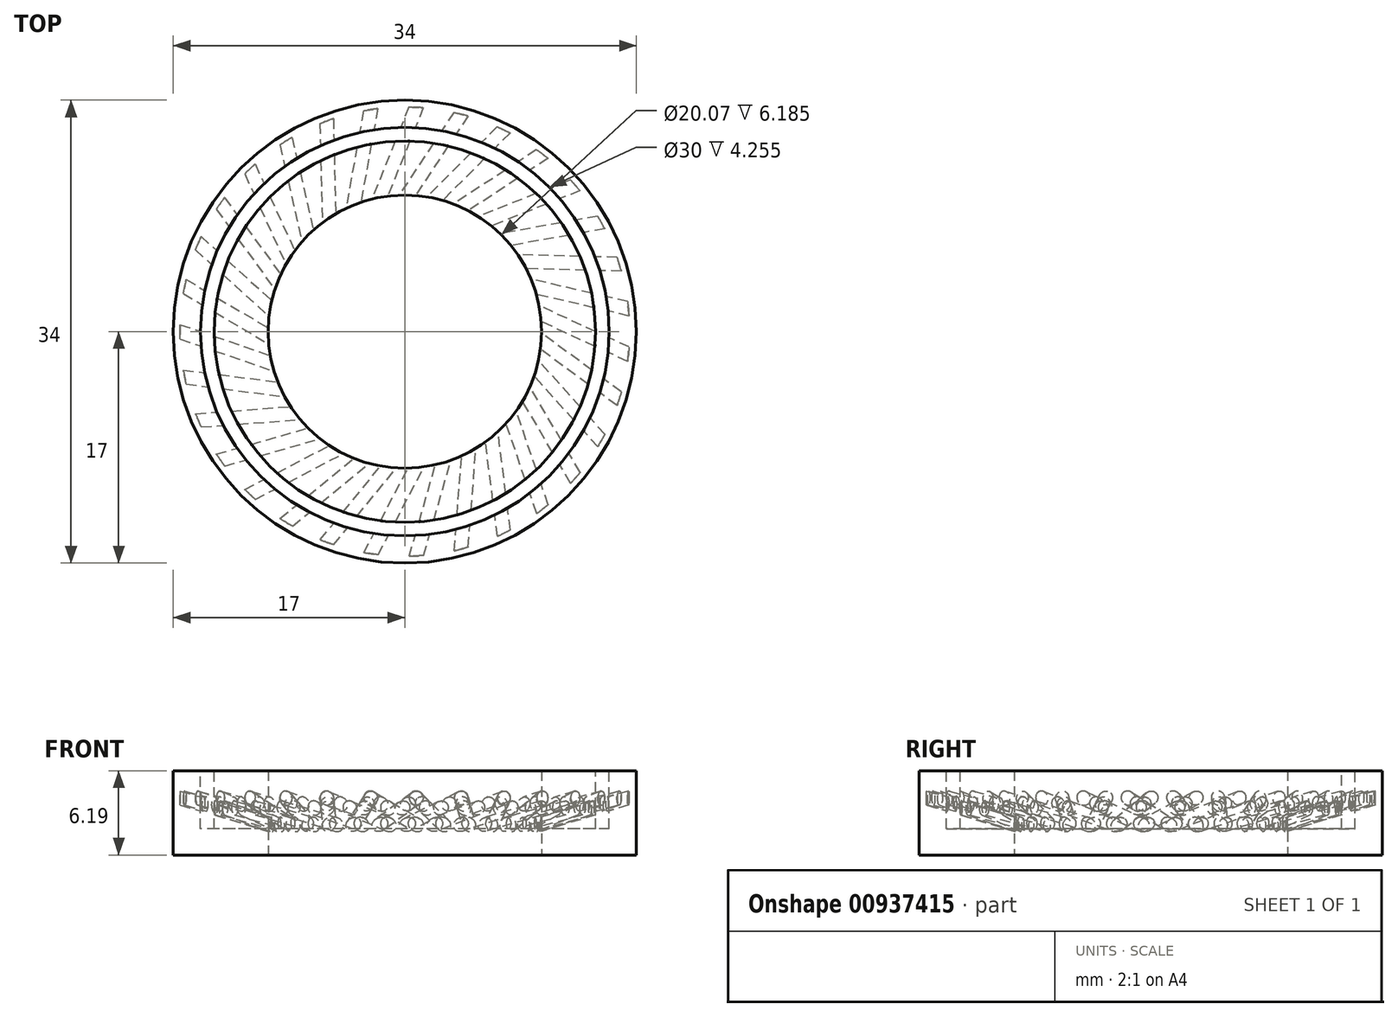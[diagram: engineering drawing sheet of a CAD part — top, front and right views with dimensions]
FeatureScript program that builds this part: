
annotation { "Feature Type Name" : "Feature", "Feature Type Description" : "" }
export const myFeature = defineFeature(function(context is Context, id is Id, definition is map)
    precondition{}
    {
        {
            var Q0;
            Q0=qCreatedBy(makeId("Top.planeOp"),FACE);
            var sketch = newSketch(context, id + "F0", { "sketchPlane" : qUnion([Q0])});
            skCircle(sketch, "E0", {"center": v(0, 0) * mm, "radius": 16.5 * mm});
            skSolve(sketch);
        }
        {
            var Q0;
            Q0=makeQuery(id+"F0.imprint","IMPRINT",FACE,{"disambiguationData":[TD([[makeQuery(id+"F0.imprint","IMPRINT",EDGE,{"derivedFrom":sQuery(id+"F0.wireOp",EDGE,"E0")}),1.0]])]});
            extrude(context, id + "F1", {"entities" : qUnion([Q0]), "depth" : 7.94 * mm, "offsetDistance" : 25.4 * mm});
        }
        {
            var Q0;
            Q0=qCreatedBy(makeId("Top.planeOp"),FACE);
            var sketch = newSketch(context, id + "F2", { "sketchPlane" : qUnion([Q0])});
            skCircle(sketch, "E1", {"center": v(0, 0) * mm, "radius": 10.03 * mm});
            skSolve(sketch);
        }
        {
            var Q0;
            Q0=qSketchRegion(id+"F2",true);
            extrude(context, id + "F3", {"entities" : qUnion([Q0]), "operationType" : NewBodyOperationType.REMOVE, "depth" : 7.94 * mm, "offsetDistance" : 25.4 * mm});
        }
        {
            var Q0;
            Q0=qCreatedBy(makeId("Right.planeOp"),FACE);
            var sketch = newSketch(context, id + "F4", { "sketchPlane" : qUnion([Q0])});
            skLineSegment(sketch, "E2", {"start": v(0, 0) * mm, "end": v(0, 143.33) * mm});
            skLineSegment(sketch, "E3", {"start": v(-8.9, 0) * mm, "end": v(-8.9, 70.97) * mm});
            skSolve(sketch);
        }
        {
            var Q0;
            Q0=qCreatedBy(makeId("Top.planeOp"),FACE);
            var sketch = newSketch(context, id + "F5", { "sketchPlane" : qUnion([Q0])});
            skLineSegment(sketch, "E4", {"start": v(0, 0) * mm, "end": v(29.86, 0) * mm});
            skSolve(sketch);
        }
        {
            var Q0;
            Q0=qCreatedBy(makeId("Right.planeOp"),FACE);
            var sketch = newSketch(context, id + "F6", { "sketchPlane" : qUnion([Q0])});
            skCircle(sketch, "E5", {"center": v(0, 54.1) * mm, "radius": 0.5 * mm});
            skSolve(sketch);
        }
        {
            var Q0;
            Q0=makeQuery(id+"F6.imprint","IMPRINT",FACE,{"disambiguationData":[TD([[makeQuery(id+"F6.imprint","IMPRINT",EDGE,{"derivedFrom":sQuery(id+"F6.wireOp",EDGE,"E5")}),1.0]])]});
            extrude(context, id + "F7", {"entities" : qUnion([Q0]), "depth" : 25.4 * mm, "offsetDistance" : 25.4 * mm});
        }
        {
            var Q0;
            Q0=makeQuery(id+"F7.opExtrude","SWEPT_BODY",BODY,{"disambiguationData":[OSD([sQuery(id+"F6.wireOp",EDGE,"E5")])]});
            var Q1;
            Q1=sQuery(id+"F4.wireOp",EDGE,"E2");
            transform(context, id + "F8", {"entities" : qUnion([Q0]), "transformType" : TransformType.ROTATION, "transformAxis" : qUnion([Q1]), "angle" : 20 * degree, "makeCopy" : false});
        }
        {
            var Q0;
            Q0=makeQuery(id+"F7.opExtrude","SWEPT_BODY",BODY,{"disambiguationData":[OSD([sQuery(id+"F6.wireOp",EDGE,"E5")])]});
            transform(context, id + "F9", {"entities" : qUnion([Q0]), "transformType" : TransformType.TRANSLATION_3D, "dx" : 0 * mm, "dy" : 0 * mm, "dz" : -54.1 * mm, "makeCopy" : false});
        }
        {
            var Q0;
            Q0=makeQuery(id+"F7.opExtrude","SWEPT_BODY",BODY,{"disambiguationData":[OSD([sQuery(id+"F6.wireOp",EDGE,"E5")])]});
            var Q1;
            Q1=sQuery(id+"F5.wireOp",EDGE,"E4");
            var Q2;
            Q2=sQuery(id+"F5.wireOp",EDGE,"E4");
            transform(context, id + "F10", {"entities" : qUnion([Q0]), "transformType" : TransformType.ROTATION, "transformAxis" : qUnion([Q2]), "angle" : 50 * degree, "makeCopy" : false});
        }
        {
            var Q0;
            Q0=makeQuery(id+"F7.opExtrude","SWEPT_BODY",BODY,{"disambiguationData":[OSD([sQuery(id+"F6.wireOp",EDGE,"E5")])]});
            var Q1;
            Q1=sQuery(id+"F4.wireOp",EDGE,"E2");
            var Q2;
            Q2=sQuery(id+"F4.wireOp",EDGE,"E3");
            transform(context, id + "F11", {"entities" : qUnion([Q0]), "transformType" : TransformType.ROTATION, "transformAxis" : qUnion([Q2]), "angle" : 55 * degree, "makeCopy" : false});
        }
        {
            var Q0;
            Q0=makeQuery(id+"F7.opExtrude","SWEPT_BODY",BODY,{"disambiguationData":[OSD([sQuery(id+"F6.wireOp",EDGE,"E5")])]});
            var Q1;
            Q1=sQuery(id+"F4.wireOp",EDGE,"E2");
            circularPattern(context, id + "F12", {"entities" : qUnion([Q0]), "axis" : qUnion([Q1]), "angle" : 360 * degree, "instanceCount" : 31, "equalSpace" : true});
        }
        {
            var Q0;
            Q0=makeQuery(id+"F7.opExtrude","SWEPT_BODY",BODY,{"disambiguationData":[OSD([sQuery(id+"F6.wireOp",EDGE,"E5")])]});
            var Q1;
            Q1=makeQuery(id+"F12.opPattern","COPY",BODY,{"derivedFrom":makeQuery(id+"F7.opExtrude","SWEPT_BODY",BODY,{"disambiguationData":[OSD([sQuery(id+"F6.wireOp",EDGE,"E5")])]}),"instanceName":"14"});
            var Q2;
            Q2=makeQuery(id+"F1.opExtrude","SWEPT_BODY",BODY,{"disambiguationData":[OSD([sQuery(id+"F0.wireOp",EDGE,"E0")])]});
            booleanBodies(context, id + "F13", {"operationType" : BooleanOperationType.SUBTRACTION, "tools" : qUnion([Q0, Q1]), "targets" : qUnion([Q2])});
        }
        {
            var Q0;
            Q0=makeQuery(id+"F12.opPattern","COPY",BODY,{"derivedFrom":makeQuery(id+"F7.opExtrude","SWEPT_BODY",BODY,{"disambiguationData":[OSD([sQuery(id+"F6.wireOp",EDGE,"E5")])]}),"instanceName":"30"});
            var Q1;
            Q1=makeQuery(id+"F12.opPattern","COPY",BODY,{"derivedFrom":makeQuery(id+"F7.opExtrude","SWEPT_BODY",BODY,{"disambiguationData":[OSD([sQuery(id+"F6.wireOp",EDGE,"E5")])]}),"instanceName":"28"});
            var Q2;
            Q2=makeQuery(id+"F12.opPattern","COPY",BODY,{"derivedFrom":makeQuery(id+"F7.opExtrude","SWEPT_BODY",BODY,{"disambiguationData":[OSD([sQuery(id+"F6.wireOp",EDGE,"E5")])]}),"instanceName":"26"});
            var Q3;
            Q3=makeQuery(id+"F12.opPattern","COPY",BODY,{"derivedFrom":makeQuery(id+"F7.opExtrude","SWEPT_BODY",BODY,{"disambiguationData":[OSD([sQuery(id+"F6.wireOp",EDGE,"E5")])]}),"instanceName":"24"});
            var Q4;
            Q4=makeQuery(id+"F12.opPattern","COPY",BODY,{"derivedFrom":makeQuery(id+"F7.opExtrude","SWEPT_BODY",BODY,{"disambiguationData":[OSD([sQuery(id+"F6.wireOp",EDGE,"E5")])]}),"instanceName":"22"});
            var Q5;
            Q5=makeQuery(id+"F1.opExtrude","SWEPT_BODY",BODY,{"disambiguationData":[OSD([sQuery(id+"F0.wireOp",EDGE,"E0")])]});
            booleanBodies(context, id + "F14", {"operationType" : BooleanOperationType.SUBTRACTION, "tools" : qUnion([Q0, Q1, Q2, Q3, Q4]), "targets" : qUnion([Q5])});
        }
        {
            var Q0;
            Q0=makeQuery(id+"F12.opPattern","COPY",BODY,{"derivedFrom":makeQuery(id+"F7.opExtrude","SWEPT_BODY",BODY,{"disambiguationData":[OSD([sQuery(id+"F6.wireOp",EDGE,"E5")])]}),"instanceName":"20"});
            var Q1;
            Q1=makeQuery(id+"F12.opPattern","COPY",BODY,{"derivedFrom":makeQuery(id+"F7.opExtrude","SWEPT_BODY",BODY,{"disambiguationData":[OSD([sQuery(id+"F6.wireOp",EDGE,"E5")])]}),"instanceName":"18"});
            var Q2;
            Q2=makeQuery(id+"F12.opPattern","COPY",BODY,{"derivedFrom":makeQuery(id+"F7.opExtrude","SWEPT_BODY",BODY,{"disambiguationData":[OSD([sQuery(id+"F6.wireOp",EDGE,"E5")])]}),"instanceName":"16"});
            var Q3;
            Q3=makeQuery(id+"F12.opPattern","COPY",BODY,{"derivedFrom":makeQuery(id+"F7.opExtrude","SWEPT_BODY",BODY,{"disambiguationData":[OSD([sQuery(id+"F6.wireOp",EDGE,"E5")])]}),"instanceName":"13"});
            var Q4;
            Q4=makeQuery(id+"F12.opPattern","COPY",BODY,{"derivedFrom":makeQuery(id+"F7.opExtrude","SWEPT_BODY",BODY,{"disambiguationData":[OSD([sQuery(id+"F6.wireOp",EDGE,"E5")])]}),"instanceName":"11"});
            var Q5;
            Q5=makeQuery(id+"F12.opPattern","COPY",BODY,{"derivedFrom":makeQuery(id+"F7.opExtrude","SWEPT_BODY",BODY,{"disambiguationData":[OSD([sQuery(id+"F6.wireOp",EDGE,"E5")])]}),"instanceName":"9"});
            var Q6;
            Q6=makeQuery(id+"F12.opPattern","COPY",BODY,{"derivedFrom":makeQuery(id+"F7.opExtrude","SWEPT_BODY",BODY,{"disambiguationData":[OSD([sQuery(id+"F6.wireOp",EDGE,"E5")])]}),"instanceName":"7"});
            var Q7;
            Q7=makeQuery(id+"F12.opPattern","COPY",BODY,{"derivedFrom":makeQuery(id+"F7.opExtrude","SWEPT_BODY",BODY,{"disambiguationData":[OSD([sQuery(id+"F6.wireOp",EDGE,"E5")])]}),"instanceName":"5"});
            var Q8;
            Q8=makeQuery(id+"F12.opPattern","COPY",BODY,{"derivedFrom":makeQuery(id+"F7.opExtrude","SWEPT_BODY",BODY,{"disambiguationData":[OSD([sQuery(id+"F6.wireOp",EDGE,"E5")])]}),"instanceName":"3"});
            var Q9;
            Q9=makeQuery(id+"F12.opPattern","COPY",BODY,{"derivedFrom":makeQuery(id+"F7.opExtrude","SWEPT_BODY",BODY,{"disambiguationData":[OSD([sQuery(id+"F6.wireOp",EDGE,"E5")])]}),"instanceName":"1"});
            var Q10;
            Q10=makeQuery(id+"F1.opExtrude","SWEPT_BODY",BODY,{"disambiguationData":[OSD([sQuery(id+"F0.wireOp",EDGE,"E0")])]});
            booleanBodies(context, id + "F15", {"operationType" : BooleanOperationType.SUBTRACTION, "tools" : qUnion([Q0, Q1, Q2, Q3, Q4, Q5, Q6, Q7, Q8, Q9]), "targets" : qUnion([Q10])});
        }
        {
            var Q0;
            Q0=makeQuery(id+"F12.opPattern","COPY",BODY,{"derivedFrom":makeQuery(id+"F7.opExtrude","SWEPT_BODY",BODY,{"disambiguationData":[OSD([sQuery(id+"F6.wireOp",EDGE,"E5")])]}),"instanceName":"29"});
            var Q1;
            Q1=makeQuery(id+"F12.opPattern","COPY",BODY,{"derivedFrom":makeQuery(id+"F7.opExtrude","SWEPT_BODY",BODY,{"disambiguationData":[OSD([sQuery(id+"F6.wireOp",EDGE,"E5")])]}),"instanceName":"27"});
            var Q2;
            Q2=makeQuery(id+"F12.opPattern","COPY",BODY,{"derivedFrom":makeQuery(id+"F7.opExtrude","SWEPT_BODY",BODY,{"disambiguationData":[OSD([sQuery(id+"F6.wireOp",EDGE,"E5")])]}),"instanceName":"25"});
            var Q3;
            Q3=makeQuery(id+"F12.opPattern","COPY",BODY,{"derivedFrom":makeQuery(id+"F7.opExtrude","SWEPT_BODY",BODY,{"disambiguationData":[OSD([sQuery(id+"F6.wireOp",EDGE,"E5")])]}),"instanceName":"23"});
            var Q4;
            Q4=makeQuery(id+"F12.opPattern","COPY",BODY,{"derivedFrom":makeQuery(id+"F7.opExtrude","SWEPT_BODY",BODY,{"disambiguationData":[OSD([sQuery(id+"F6.wireOp",EDGE,"E5")])]}),"instanceName":"21"});
            var Q5;
            Q5=makeQuery(id+"F12.opPattern","COPY",BODY,{"derivedFrom":makeQuery(id+"F7.opExtrude","SWEPT_BODY",BODY,{"disambiguationData":[OSD([sQuery(id+"F6.wireOp",EDGE,"E5")])]}),"instanceName":"19"});
            var Q6;
            Q6=makeQuery(id+"F12.opPattern","COPY",BODY,{"derivedFrom":makeQuery(id+"F7.opExtrude","SWEPT_BODY",BODY,{"disambiguationData":[OSD([sQuery(id+"F6.wireOp",EDGE,"E5")])]}),"instanceName":"17"});
            var Q7;
            Q7=makeQuery(id+"F12.opPattern","COPY",BODY,{"derivedFrom":makeQuery(id+"F7.opExtrude","SWEPT_BODY",BODY,{"disambiguationData":[OSD([sQuery(id+"F6.wireOp",EDGE,"E5")])]}),"instanceName":"15"});
            var Q8;
            Q8=makeQuery(id+"F12.opPattern","COPY",BODY,{"derivedFrom":makeQuery(id+"F7.opExtrude","SWEPT_BODY",BODY,{"disambiguationData":[OSD([sQuery(id+"F6.wireOp",EDGE,"E5")])]}),"instanceName":"12"});
            var Q9;
            Q9=makeQuery(id+"F12.opPattern","COPY",BODY,{"derivedFrom":makeQuery(id+"F7.opExtrude","SWEPT_BODY",BODY,{"disambiguationData":[OSD([sQuery(id+"F6.wireOp",EDGE,"E5")])]}),"instanceName":"10"});
            var Q10;
            Q10=makeQuery(id+"F12.opPattern","COPY",BODY,{"derivedFrom":makeQuery(id+"F7.opExtrude","SWEPT_BODY",BODY,{"disambiguationData":[OSD([sQuery(id+"F6.wireOp",EDGE,"E5")])]}),"instanceName":"8"});
            var Q11;
            Q11=makeQuery(id+"F12.opPattern","COPY",BODY,{"derivedFrom":makeQuery(id+"F7.opExtrude","SWEPT_BODY",BODY,{"disambiguationData":[OSD([sQuery(id+"F6.wireOp",EDGE,"E5")])]}),"instanceName":"6"});
            var Q12;
            Q12=makeQuery(id+"F12.opPattern","COPY",BODY,{"derivedFrom":makeQuery(id+"F7.opExtrude","SWEPT_BODY",BODY,{"disambiguationData":[OSD([sQuery(id+"F6.wireOp",EDGE,"E5")])]}),"instanceName":"4"});
            var Q13;
            Q13=makeQuery(id+"F12.opPattern","COPY",BODY,{"derivedFrom":makeQuery(id+"F7.opExtrude","SWEPT_BODY",BODY,{"disambiguationData":[OSD([sQuery(id+"F6.wireOp",EDGE,"E5")])]}),"instanceName":"2"});
            var Q14;
            Q14=makeQuery(id+"F1.opExtrude","SWEPT_BODY",BODY,{"disambiguationData":[OSD([sQuery(id+"F0.wireOp",EDGE,"E0")])]});
            booleanBodies(context, id + "F16", {"operationType" : BooleanOperationType.SUBTRACTION, "tools" : qUnion([Q0, Q1, Q2, Q3, Q4, Q5, Q6, Q7, Q8, Q9, Q10, Q11, Q12, Q13]), "targets" : qUnion([Q14])});
        }
        {
            var Q0;
            Q0=makeQuery(id+"F1.opExtrude","CAP_FACE",FACE,{"disambiguationData":[OSD([sQuery(id+"F0.wireOp",EDGE,"E0")])],"isStart":true});
            var sketch = newSketch(context, id + "F17", { "sketchPlane" : qUnion([Q0])});
            skCircle(sketch, "E6", {"center": v(0, 0) * mm, "radius": 16.5 * mm});
            skSolve(sketch);
        }
        {
            var Q0;
            Q0=makeQuery(id+"F17.imprint","IMPRINT",FACE,{"disambiguationData":[TD([[makeQuery(id+"F17.imprint","IMPRINT",EDGE,{"derivedFrom":sQuery(id+"F17.wireOp",EDGE,"E6")}),-1.0]])]});
            extrude(context, id + "F18", {"entities" : qUnion([Q0]), "operationType" : NewBodyOperationType.REMOVE, "oppositeDirection" : true, "depth" : 1.75 * mm, "offsetDistance" : 25.4 * mm});
        }
        {
            var Q0;
            Q0=makeQuery(id+"F1.opExtrude","CAP_FACE",FACE,{"disambiguationData":[OSD([sQuery(id+"F0.wireOp",EDGE,"E0")])],"isStart":false});
            var sketch = newSketch(context, id + "F19", { "sketchPlane" : qUnion([Q0])});
            skCircle(sketch, "E7", {"center": v(0, 0) * mm, "radius": 15 * mm});
            skCircle(sketch, "E8", {"center": v(0, 0) * mm, "radius": 14 * mm});
            skSolve(sketch);
        }
        {
            var Q0;
            Q0=makeQuery(id+"F19.imprint","IMPRINT",FACE,{"disambiguationData":[TD([[makeQuery(id+"F19.imprint","IMPRINT",EDGE,{"derivedFrom":sQuery(id+"F19.wireOp",EDGE,"E7")}),1.0]])]});
            var Q1;
            Q1=sQuery(id+"F19.wireOp",EDGE,"E7");
            var Q2;
            Q2=sQuery(id+"F19.wireOp",EDGE,"E8");
            extrude(context, id + "F20", {"entities" : qUnion([Q0]), "operationType" : NewBodyOperationType.REMOVE, "surfaceEntities" : qUnion([Q1, Q2]), "oppositeDirection" : true, "depth" : 4.25 * mm, "offsetDistance" : 25.4 * mm});
        }
        {
            var Q0;
            {var subQ0=sQuery(id+"F0.wireOp",EDGE,"E0");Q0=makeQuery(id+"F20.boolean.opBoolean","SPLIT",FACE,{"disambiguationData":[TD([makeQuery(id+"F1.opExtrude","SWEPT_FACE",FACE,{"disambiguationData":[OSD([subQ0])]})])],"derivedFrom":makeQuery(id+"F1.opExtrude","CAP_FACE",FACE,{"disambiguationData":[OSD([subQ0])],"isStart":false})});}
            var sketch = newSketch(context, id + "F21", { "sketchPlane" : qUnion([Q0])});
            skCircle(sketch, "E9", {"center": v(0, 0) * mm, "radius": 17 * mm});
            skSolve(sketch);
        }
        {
            var Q0;
            Q0=makeQuery(id+"F21.imprint","IMPRINT",FACE,{"disambiguationData":[TD([[makeQuery(id+"F21.imprint","IMPRINT",EDGE,{"derivedFrom":sQuery(id+"F21.wireOp",EDGE,"E9")}),1.0]])]});
            var Q1;
            Q1=makeQuery(id+"F18.boolean.opBoolean","COPY",FACE,{"derivedFrom":makeQuery(id+"F18.opExtrude","CAP_FACE",FACE,{"disambiguationData":[OSD([sQuery(id+"F2.wireOp",EDGE,"E1"),sQuery(id+"F17.wireOp",EDGE,"E6")])],"isStart":false})});
            var Q2;
            Q2=makeQuery(id+"F1.opExtrude","SWEPT_BODY",BODY,{"disambiguationData":[OSD([sQuery(id+"F0.wireOp",EDGE,"E0")])]});
            extrude(context, id + "F22", {"entities" : qUnion([Q0]), "operationType" : NewBodyOperationType.ADD, "endBound" : BoundingType.UP_TO_SURFACE, "oppositeDirection" : true, "depth" : 4.7 * mm, "endBoundEntityFace" : qUnion([Q1]), "endBoundEntityBody" : qUnion([Q2]), "offsetDistance" : 25.4 * mm});
        }
    });
